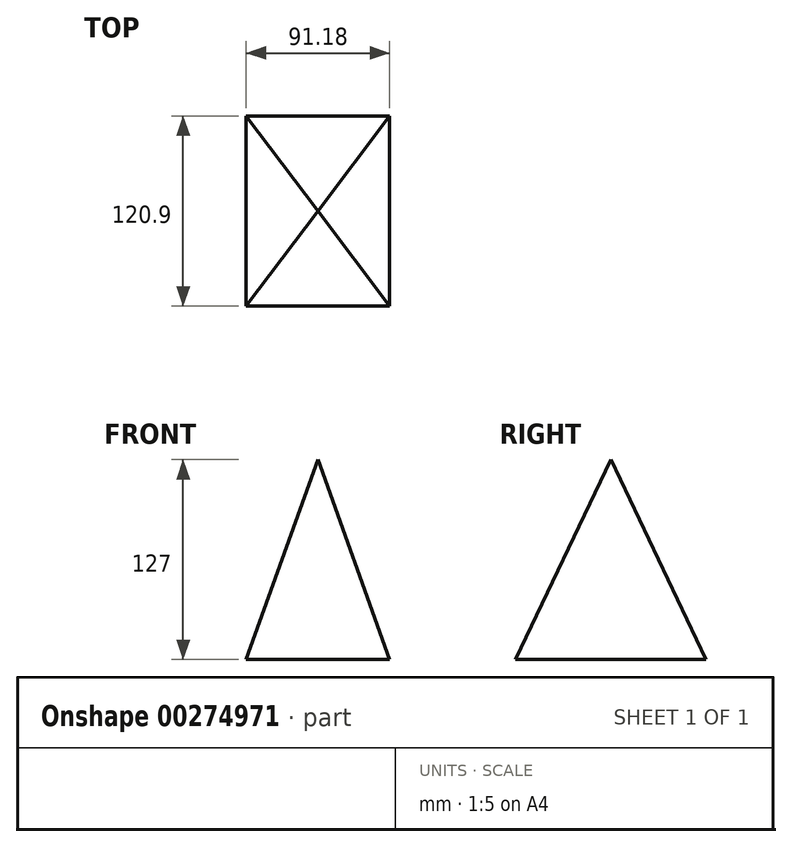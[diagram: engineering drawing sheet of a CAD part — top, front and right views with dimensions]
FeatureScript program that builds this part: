
annotation { "Feature Type Name" : "Feature", "Feature Type Description" : "" }
export const myFeature = defineFeature(function(context is Context, id is Id, definition is map)
    precondition{}
    {
        {
            var Q0;
            Q0=qCreatedBy(makeId("Top.planeOp"),FACE);
            var sketch = newSketch(context, id + "F0", { "sketchPlane" : qUnion([Q0])});
            skLineSegment(sketch, "E0.bottom", {"start": v(45.59, 60.45) * mm, "end": v(-45.59, 60.45) * mm});
            skLineSegment(sketch, "E0.top", {"start": v(45.59, -60.45) * mm, "end": v(-45.59, -60.45) * mm});
            skLineSegment(sketch, "E0.left", {"start": v(45.59, 60.45) * mm, "end": v(45.59, -60.45) * mm});
            skLineSegment(sketch, "E0.right", {"start": v(-45.59, 60.45) * mm, "end": v(-45.59, -60.45) * mm});
            skPoint(sketch, "E0.middle", {"position": v(0, 0) * mm});
            skSolve(sketch);
        }
        {
            var Q0;
            Q0=qCreatedBy(makeId("Top.planeOp"),FACE);
            cPlane(context, id + "F1", {"entities" : qUnion([Q0]), "cplaneType" : CPlaneType.OFFSET, "offset" : 127 * mm, "width" : 152.4 * mm, "height" : 152.4 * mm});
        }
        {
            var Q0;
            Q0=qCreatedBy(id+"F1.planeOp",FACE);
            var sketch = newSketch(context, id + "F2", { "sketchPlane" : qUnion([Q0])});
            skPoint(sketch, "E1.middle", {"position": v(0, 0) * mm});
            skCircle(sketch, "E2", {"center": v(0, 0) * mm, "radius": 31.3 * mm});
            skSolve(sketch);
        }
        {
            var Q0;
            Q0=sQuery(id+"F2.wireOp",VERTEX,"E1.middle");
            var Q1;
            Q1=makeQuery(id+"F0.imprint","IMPRINT",FACE,{"disambiguationData":[TD([[makeQuery(id+"F0.imprint","IMPRINT",EDGE,{"derivedFrom":sQuery(id+"F0.wireOp",EDGE,"E0.bottom")}),1.0]])]});
            loft(context, id + "F3", {"sheetProfilesArray" : [{ "sheetProfileEntities" : qUnion([Q0]) }, { "sheetProfileEntities" : qUnion([Q1]) }]});
        }
    });
